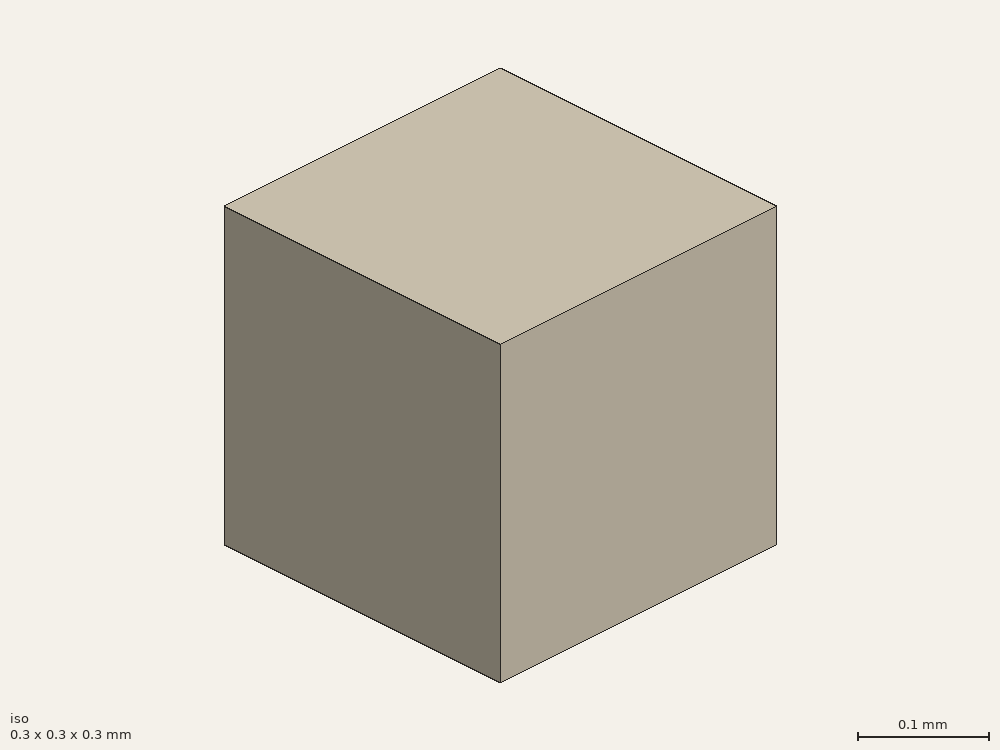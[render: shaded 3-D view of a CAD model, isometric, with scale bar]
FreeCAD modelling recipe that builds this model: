
FCSTD DOCUMENT  (FreeCAD 0.21R33694 (Git))
Label: square-planar
License: All rights reserved
LicenseURL: http://en.wikipedia.org/wiki/All_rights_reserved
objects: Part::Part2DObjectPython×18, App::FeaturePython×9, Part::Extrusion×8, Part::Cut×6, Part::FeaturePython×2
note: 34 computed .brp shape members not serialized (recipe doc carries the construction recipe); baked Part::Feature solids carry a one-line shape summary decoded from their .brp

FEATURE [Part::Part2DObjectPython] Rectangle  label="gp2D"  # Draft 2D object (typed FeaturePython)
  Area = 22500
  ChamferSize = 0
  Columns = 1
  FilletRadius = 0
  Height = 150
  Length = 150
  MakeFace = true
  Placement = pos=(-75,-75,0) rot=(0,0,1;0rad)
  Rows = 1
FEATURE [Part::Part2DObjectPython] Polygon  label="inner2D"  # Draft 2D object (typed FeaturePython)
  Area = 1.10213
  ChamferSize = 0
  DrawMode = 0
  FacesNumber = 16
  FilletRadius = 0
  MakeFace = true
  Radius = 0.6
FEATURE [Part::Part2DObjectPython] Polygon001  label="outer2D"  # Draft 2D object (typed FeaturePython)
  Area = 13.1181
  ChamferSize = 0
  DrawMode = 0
  FacesNumber = 16
  FilletRadius = 0
  MakeFace = true
  Radius = 2.07
FEATURE [Part::Part2DObjectPython] Polygon002  label="barrel2D"  # Draft 2D object (typed FeaturePython)
  Area = 27.5532
  ChamferSize = 0
  DrawMode = 0
  FacesNumber = 16
  FilletRadius = 0
  MakeFace = true
  Radius = 3
FEATURE [Part::Part2DObjectPython] Clone2D  label="inner2D (2D)"  # Draft 2D object (typed FeaturePython)
  Fuse = false
  Objects = -> [Polygon]
  Scale = (1,1,1)
FEATURE [Part::Extrusion] Extrude001  label="coax-pin"
  Base = -> Clone2D
  Dir = (0,0,1)
  DirMode = 2
  FaceMakerClass = Part::FaceMakerBullseye
  LengthFwd = -1
  LengthRev = 0
  Solid = false
  Symmetric = false
FEATURE [Part::Extrusion] Extrude002  label="coax-dielectic"
  Base = -> Polygon001
  Dir = (0,0,1)
  DirMode = 2
  FaceMakerClass = Part::FaceMakerBullseye
  LengthFwd = -1
  LengthRev = 0
  Solid = false
  Symmetric = false
FEATURE [Part::Extrusion] Extrude003  label="coax-outer"
  Base = -> Polygon002
  Dir = (0,0,1)
  DirMode = 2
  FaceMakerClass = Part::FaceMakerBullseye
  LengthFwd = -2
  LengthRev = 0
  Solid = false
  Symmetric = false
FEATURE [Part::Cut] Cut001  label="teflon"
  Base = -> Extrude002
  Tool = -> Extrude001
FEATURE [Part::Extrusion] Extrude004
  Base = -> Rectangle
  Dir = (0,0,1)
  DirMode = 2
  FaceMakerClass = Part::FaceMakerBullseye
  LengthFwd = -0.2
  LengthRev = 0
  Solid = false
  Symmetric = false
FEATURE [Part::Part2DObjectPython] Clone2D001  label="barrel2D (2D)"  # Draft 2D object (typed FeaturePython)
  Fuse = false
  Objects = -> [Polygon002]
  Scale = (1,1,1)
FEATURE [Part::Extrusion] Extrude005
  Base = -> Clone2D001
  Dir = (0,0,1)
  DirMode = 2
  FaceMakerClass = Part::FaceMakerBullseye
  LengthFwd = -5
  LengthRev = 0
  Solid = false
  Symmetric = false
FEATURE [Part::Part2DObjectPython] Rectangle003  label="air2D"  # Draft 2D object (typed FeaturePython)
  Area = 90000
  ChamferSize = 0
  Columns = 1
  FilletRadius = 0
  Height = 300
  Length = 300
  MakeFace = true
  Placement = pos=(-150,-150,0) rot=(0,0,1;0rad)
  Rows = 1
FEATURE [Part::Part2DObjectPython] Wire  label="_Pport"  # Draft 2D object (typed FeaturePython)
  Area = 1.31181e-05
  ChamferSize = 0
  Closed = true
  End = (4e-16,-0.00207,-0.001)
  FilletRadius = 0
  Length = 0.0129228
  MakeFace = true
  Placement = pos=(0.000792155,-0.00191243,-0.001) rot=(0,0,1;0rad)
  Points = (16) [(0,0,0),(0.000671556,0.00044872,0),(0.00112028,0.00112028,0),(0.00127785,0.00191243,0),(0.00112028,0.00270459,0),(0.000671556,0.00337614,0),+10 more]
  Start = (0.000792155,-0.00191243,-0.001)
  Subdivisions = 0
FEATURE [Part::Part2DObjectPython] Wire001  label="_Pi"  # Draft 2D object (typed FeaturePython)
  Area = 1.10213e-06
  ChamferSize = 0
  Closed = true
  End = (0.00022961,-0.000554328,-0.001)
  FilletRadius = 0
  Length = 0.00374573
  MakeFace = true
  Placement = pos=(0.000424264,-0.000424264,-0.001) rot=(0,0,1;0rad)
  Points = (16) [(0,0,0),(0.000130064,0.000194654,0),(0.000175736,0.000424264,0),(0.000130064,0.000653874,0),(0,0.000848528,0),(-0.000194654,0.000978592,0),+10 more]
  Start = (0.000424264,-0.000424264,-0.001)
  Subdivisions = 0
FEATURE [Part::Part2DObjectPython] Line  label="_Pv"  # Draft 2D object (typed FeaturePython)
  Area = 0
  ChamferSize = 0
  Closed = false
  End = (0.000424264,-0.000424264,-0.001)
  FilletRadius = 0
  Length = 0.00147
  MakeFace = true
  Placement = pos=(0.00146371,-0.00146371,-0.001) rot=(0,0,1;0rad)
  Points = (2) [(0,0,0),(-0.00103945,0.00103945,0)]
  Start = (0.00146371,-0.00146371,-0.001)
  Subdivisions = 0
FEATURE [App::FeaturePython] Text  label="_Btop(radiation){top}"  # WARN: FeaturePython — macro-defined, semantics opaque (R4)
  Placement = pos=(0.308621,-0.303467,0.3) rot=(0,0,1;0rad)
  Text = .
FEATURE [App::FeaturePython] Text001  label="_Bfront(radiation){front}"  # WARN: FeaturePython — macro-defined, semantics opaque (R4)
  Placement = pos=(0.308621,-0.303467,0.3) rot=(0,0,1;0rad)
  Text = .
FEATURE [App::FeaturePython] Text002  label="_Bright(radiation){right}"  # WARN: FeaturePython — macro-defined, semantics opaque (R4)
  Placement = pos=(0.308621,-0.303467,0.3) rot=(0,0,1;0rad)
  Text = .
FEATURE [App::FeaturePython] Text003  label="_Bleft(radiation){left}"  # WARN: FeaturePython — macro-defined, semantics opaque (R4)
  Placement = pos=(0.308621,-0.303467,0.3) rot=(0,0,1;0rad)
  Text = .
FEATURE [App::FeaturePython] Text004  label="_Bback(radiation){back}"  # WARN: FeaturePython — macro-defined, semantics opaque (R4)
  Placement = pos=(0.308621,-0.303467,0.3) rot=(0,0,1;0rad)
  Text = .
FEATURE [App::FeaturePython] Text005  label="_Bbottom(radiation){bottom}"  # WARN: FeaturePython — macro-defined, semantics opaque (R4)
  Placement = pos=(0.308621,-0.303467,0.3) rot=(0,0,1;0rad)
  Text = .
FEATURE [App::FeaturePython] Text006  label="_Sin(PV){port}"  # WARN: FeaturePython — macro-defined, semantics opaque (R4)
  Placement = pos=(0.308621,-0.303467,0.3) rot=(0,0,1;0rad)
  Text = .
FEATURE [App::FeaturePython] Text007  label="_Min(1,voltage){v}"  # WARN: FeaturePython — macro-defined, semantics opaque (R4)
  Placement = pos=(0.308621,-0.303467,0.3) rot=(0,0,1;0rad)
  Text = .
FEATURE [App::FeaturePython] Text008  label="_Min(1,current){i}"  # WARN: FeaturePython — macro-defined, semantics opaque (R4)
  Placement = pos=(0.308621,-0.303467,0.3) rot=(0,0,1;0rad)
  Text = .
FEATURE [Part::Cut] Cut002  label="gp"
  Base = -> Extrude004
  Tool = -> Extrude005
FEATURE [Part::Part2DObjectPython] Rectangle010  label="antenna2D"  # Draft 2D object (typed FeaturePython)
  Area = 1600
  ChamferSize = 0
  Columns = 1
  FilletRadius = 0
  Height = 40
  Length = 40
  MakeFace = true
  Placement = pos=(-20,0,4.5) rot=(1,0,0;1.5708rad)
  Rows = 1
FEATURE [Part::Part2DObjectPython] Rectangle013  # Draft 2D object (typed FeaturePython)
  Area = 5
  ChamferSize = 0
  Columns = 1
  FilletRadius = 0
  Height = 2.5
  Length = 2
  MakeFace = true
  Placement = pos=(-1,0,0) rot=(1,0,0;1.5708rad)
  Rows = 1
FEATURE [Part::Extrusion] Extrude009  label="antenna"
  Base = -> Rectangle010
  Dir = (0,-1,2e-16)
  DirMode = 2
  FaceMakerClass = Part::FaceMakerBullseye
  LengthFwd = 0.2
  LengthRev = 0
  Placement = pos=(0,0.1,-2) rot=(0,0,1;0rad)
  Solid = false
  Symmetric = false
FEATURE [Part::Extrusion] Extrude  label="air"
  Base = -> Rectangle003
  Dir = (0,0,1)
  DirMode = 2
  FaceMakerClass = Part::FaceMakerBullseye
  LengthFwd = 300
  LengthRev = 0
  Placement = pos=(0,0,-110) rot=(0,0,1;0rad)
  Solid = false
  Symmetric = false
FEATURE [Part::Extrusion] Extrude010  label="feed"
  Base = -> Rectangle013
  Dir = (0,-1,2e-16)
  DirMode = 2
  FaceMakerClass = Part::FaceMakerBullseye
  LengthFwd = 0.2
  LengthRev = 0
  Placement = pos=(0,0.1,0) rot=(0,0,1;0rad)
  Solid = false
  Symmetric = false
FEATURE [Part::Part2DObjectPython] Rectangle014  label="_Pfront"  # Draft 2D object (typed FeaturePython)
  Area = 0.09
  ChamferSize = 0
  Columns = 1
  FilletRadius = 0
  Height = 0.3
  Length = 0.3
  MakeFace = true
  Placement = pos=(-0.15,-0.15,-0.11) rot=(1,0,0;1.5708rad)
  Rows = 1
FEATURE [Part::Part2DObjectPython] Rectangle015  label="_Pback"  # Draft 2D object (typed FeaturePython)
  Area = 0.09
  ChamferSize = 0
  Columns = 1
  FilletRadius = 0
  Height = 0.3
  Length = 0.3
  MakeFace = true
  Placement = pos=(-0.15,0.15,-0.11) rot=(1,0,0;1.5708rad)
  Rows = 1
FEATURE [Part::Part2DObjectPython] Rectangle016  label="_Ptop"  # Draft 2D object (typed FeaturePython)
  Area = 0.09
  ChamferSize = 0
  Columns = 1
  FilletRadius = 0
  Height = 0.3
  Length = 0.3
  MakeFace = true
  Placement = pos=(-0.15,-0.15,0.19) rot=(0,0,1;0rad)
  Rows = 1
FEATURE [Part::Part2DObjectPython] Rectangle017  label="_Pbottom"  # Draft 2D object (typed FeaturePython)
  Area = 0.09
  ChamferSize = 0
  Columns = 1
  FilletRadius = 0
  Height = 0.3
  Length = 0.3
  MakeFace = true
  Placement = pos=(-0.15,-0.15,-0.11) rot=(0,0,1;0rad)
  Rows = 1
FEATURE [Part::Part2DObjectPython] Rectangle018  label="_Pright"  # Draft 2D object (typed FeaturePython)
  Area = 0.09
  ChamferSize = 0
  Columns = 1
  FilletRadius = 0
  Height = 0.3
  Length = 0.3
  MakeFace = true
  Placement = pos=(0.15,-0.15,-0.11) rot=(0.57735,0.57735,0.57735;2.0944rad)
  Rows = 1
FEATURE [Part::Part2DObjectPython] Rectangle019  label="_Pleft"  # Draft 2D object (typed FeaturePython)
  Area = 0.09
  ChamferSize = 0
  Columns = 1
  FilletRadius = 0
  Height = 0.3
  Length = 0.3
  MakeFace = true
  Placement = pos=(-0.15,-0.15,-0.11) rot=(0.57735,0.57735,0.57735;2.0944rad)
  Rows = 1
FEATURE [Part::Cut] Cut
  Base = -> Extrude
  Tool = -> Extrude003
FEATURE [Part::Cut] Cut003
  Base = -> Cut
  Tool = -> Extrude010
FEATURE [Part::Cut] Cut004
  Base = -> Cut003
  Tool = -> Cut002
FEATURE [Part::Cut] Cut005
  Base = -> Cut004
  Tool = -> Extrude009
FEATURE [Part::FeaturePython] BooleanFragments  # WARN: FeaturePython — macro-defined, semantics opaque (R4)
  Mode = 0
  Objects = -> [Cut005,Cut001]
  Tolerance = 0
FEATURE [Part::FeaturePython] Clone  label="scaled"  # Draft clone (typed FeaturePython)
  AttacherType = Attacher::AttachEngine3D
  Fuse = false
  Objects = -> [BooleanFragments]
  Scale = (0.001,0.001,0.001)
